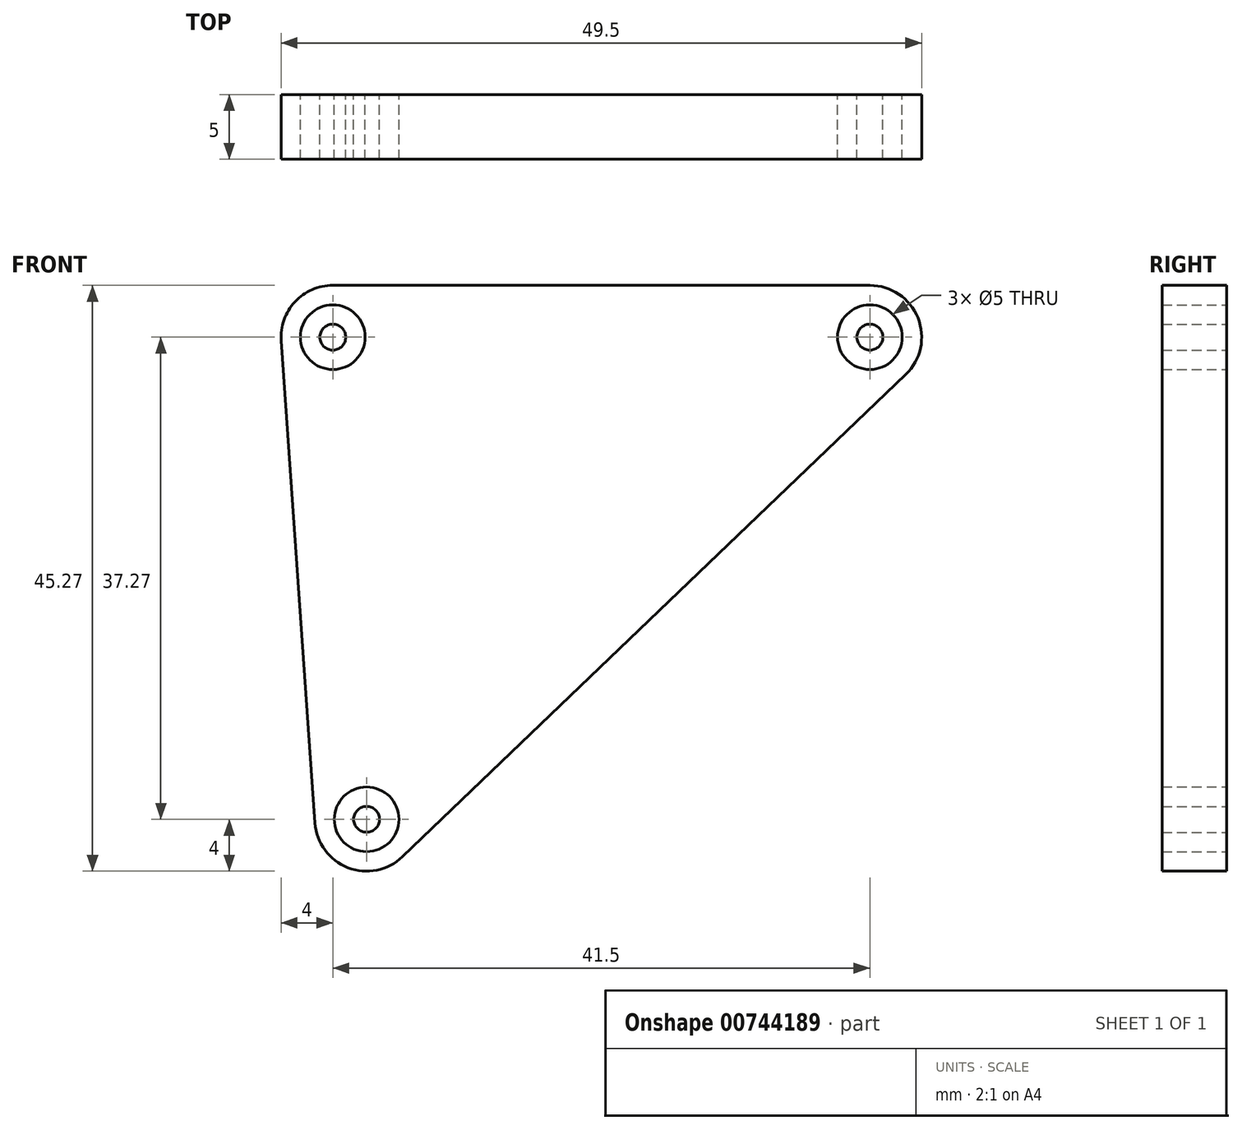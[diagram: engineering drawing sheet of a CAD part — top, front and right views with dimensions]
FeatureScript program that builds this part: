
annotation { "Feature Type Name" : "Feature", "Feature Type Description" : "" }
export const myFeature = defineFeature(function(context is Context, id is Id, definition is map)
    precondition{}
    {
        {
            var Q0;
            Q0=qCreatedBy(makeId("Front.planeOp"),FACE);
            var sketch = newSketch(context, id + "F0", { "sketchPlane" : qUnion([Q0])});
            skArc(sketch, "E0", {"start": v(-15.71, 6.74) * mm, "mid": v(-18.64, 5.47) * mm, "end": v(-19.7, 2.46) * mm});
            skArc(sketch, "E1", {"start": v(28.56, -0.15) * mm, "mid": v(29.5, 4.23) * mm, "end": v(25.79, 6.74) * mm});
            skArc(sketch, "E2", {"start": v(-17.1, -34.8) * mm, "mid": v(-14.54, -38.26) * mm, "end": v(-10.33, -37.42) * mm});
            skLineSegment(sketch, "E3", {"start": v(-15.71, 6.74) * mm, "end": v(25.79, 6.74) * mm});
            skLineSegment(sketch, "E4", {"start": v(-19.7, 2.46) * mm, "end": v(-17.1, -34.8) * mm});
            skLineSegment(sketch, "E5", {"start": v(28.56, -0.15) * mm, "end": v(-10.33, -37.42) * mm});
            skCircle(sketch, "E6", {"center": v(-15.71, 2.74) * mm, "radius": 2.5 * mm});
            skCircle(sketch, "E7", {"center": v(-15.71, 2.74) * mm, "radius": 1 * mm});
            skCircle(sketch, "E8", {"center": v(25.79, 2.74) * mm, "radius": 2.5 * mm});
            skCircle(sketch, "E9", {"center": v(25.79, 2.74) * mm, "radius": 1 * mm});
            skCircle(sketch, "E10", {"center": v(-13.1, -34.53) * mm, "radius": 1 * mm});
            skCircle(sketch, "E11", {"center": v(-13.1, -34.53) * mm, "radius": 2.5 * mm});
            skSolve(sketch);
        }
        {
            var Q0;
            Q0=qSketchRegion(id+"F0",true);
            var Q1;
            Q1=makeQuery(id+"F0.imprint","IMPRINT",FACE,{"disambiguationData":[TD([[makeQuery(id+"F0.imprint","IMPRINT",EDGE,{"derivedFrom":sQuery(id+"F0.wireOp",EDGE,"E7")}),1.0]])]});
            var Q2;
            Q2=makeQuery(id+"F0.imprint","IMPRINT",FACE,{"disambiguationData":[TD([[makeQuery(id+"F0.imprint","IMPRINT",EDGE,{"derivedFrom":sQuery(id+"F0.wireOp",EDGE,"E9")}),1.0]])]});
            var Q3;
            Q3=makeQuery(id+"F0.imprint","IMPRINT",FACE,{"disambiguationData":[TD([[makeQuery(id+"F0.imprint","IMPRINT",EDGE,{"derivedFrom":sQuery(id+"F0.wireOp",EDGE,"E10")}),1.0]])]});
            extrude(context, id + "F1", {"entities" : qUnion([Q0, Q1, Q2, Q3]), "depth" : 5 * mm, "offsetDistance" : 25 * mm});
        }
    });
